# Revit family: C1-R
name_source: partatom
category: Doors
revit_build: Autodesk Revit LT 2017 (Build: 20160225_1515(x64)
units: mm (PartAtom-declared; Revit-internal decimal feet)

## family parameters
Always vertical = Yes
Cut with Voids When Loaded = No
Host = Wall
OmniClass Number = 23.30.10.00
OmniClass Title = Doors
Room Calculation Point = No
Shared = No

## types (3) — shared parameters
6 Monthly = refer to O&M manual
Access Clearance Bottom = It is not required
Access Clearance Front = It is not required
Access Clearance Left = It is not required
Access Clearance Rear = It is not required
Access Clearance Right = It is not required
Access Clearance Top = Space above top (internal side) raccomanded 750 mm (min. 350 mm)
Analytic Construction = <Nessuno>
Annually = refer to O&M manual
AssetType = Alluser Antitailgating High Security Portals
Battery Supply = Yes
Battery Type = Sealed Lead  Acid Battery 7Ah; 12 V
CE Approval = Yes
Colour = PPC RAL 30% Gloss
Daily = refer to O&M manual
Description = Anti Tailgating High Security portal - Cylindrical Shape
Design Country = Italy
ElectricalDeviceNominalPower = 35
ExpectedLife = Subjected to regular maintenance
Feature = Anti Tailgating High Security portal - Cylindrical Shape
FireExit = No
Frequency = 50-60Hz
Function = Interior
GlassLayers = 1
HandicapAccessible = Yes
HasDrive = Yes
HasPartWinding = Yes
HasProtectiveEarth = Yes
Instruction Video = https://www.youtube.com
IsCoated = Yes
IsExternal = Yes
IsGuarded  = Yes
IsLaminated = Yes
IsWired = Yes
Location of Manufacturer = Italy
Manufacturer = Alluser Industrie srl
Manufacturer Country = Italy
Manufacturer Website = www.alluserindustrie.com
Monthly = refer to O&M manual
PhaseAngle = 0.00°
Product Model Number = C1
Product Range = High Security Portals
Product URL = https://www.alluserindustrie.com
SelfClosing = Yes
Shape = circular
Supply Phase = 1
Wall Closure = By host
Weekly = refer to O&M manual
zero-valued in all types: BeamRadiationTransmittance, ElectricMotorEfficiency, GlassThickness3, GlazingAreaFraction, Infiltration, Life Cycle Analysis, LockedRotorCurrent, MaximumPowerOutput, NominalCurrent, NominalFrequencyRange, NominalLength, NominalVoltage, Number of Poles, NumberOfPoles, Reflectivity, SolarHeatGainTransmittance, StartCurrentFactor, ThermalTransmittance, ThermalTransmittanceSummer, ThermalTransmittanceWinter, Translucency, UsageCurrent

## per-type parameters (varying)
| type | Expected Life | GlassThickness1 | GlassThickness2 | Gross Weight | Height | IsTempered | Overall Height | Overall Length | Overall Width | Radius | Radius2 | Radius3 | Radius4 | Rough Height | Shipping Weight | Size(HxWxD) | SmokeStop | Thickness | Voltage | Width |
| HUC STD | Subjected to regular maintenance | 11 mm | 0 mm  [stored 0 ft] | 360 kg (with glass P2A UNI EN 356) | 2320 mm | No | 2320 mm | 988 mm | 988 mm | 494 mm | 455 mm | 437 mm | 472 mm | 2320 mm | 490 kg (standard version: whole portal assembled, one crate) | 2312x988x988 | No | 988 mm | 110 - 230 V | 988 mm |
| HUC 2134 | subjected to regular maintenance | 5 mm  [stored 0.0164042 ft] | 5 mm  [stored 0.0164042 ft] | 375 kg (with glass P2A UNI EN 356) | 2406 mm | Yes | 2406 mm | 1151 mm | 1151 mm | 576 mm | 531 mm | 510 mm | 553 mm | 2406 mm | 515 kg (standard version: whole portal assembled, one crate) | 2406x988x988 | Yes | 1151 mm | 110 - 220 v | 1151 mm |
| HUC 2300 | Subjected to regular maintenance | 11 mm | 0 mm  [stored 0 ft] | 395 kg (with glass P2A UNI EN 356) | 2560 mm | Yes | 2560 mm | 988 mm | 988 mm | 494 mm | 455 mm | 437 mm | 472 mm | 2560 mm | 535 kg (standard version: whole portal assembled, one crate) | 2560x988x988 | Yes | 988 mm | 110 - 220 v | 988 mm |

note: [stored X ft] marks values corroborated as IEEE doubles in the binary element streams (Revit-internal decimal feet)
